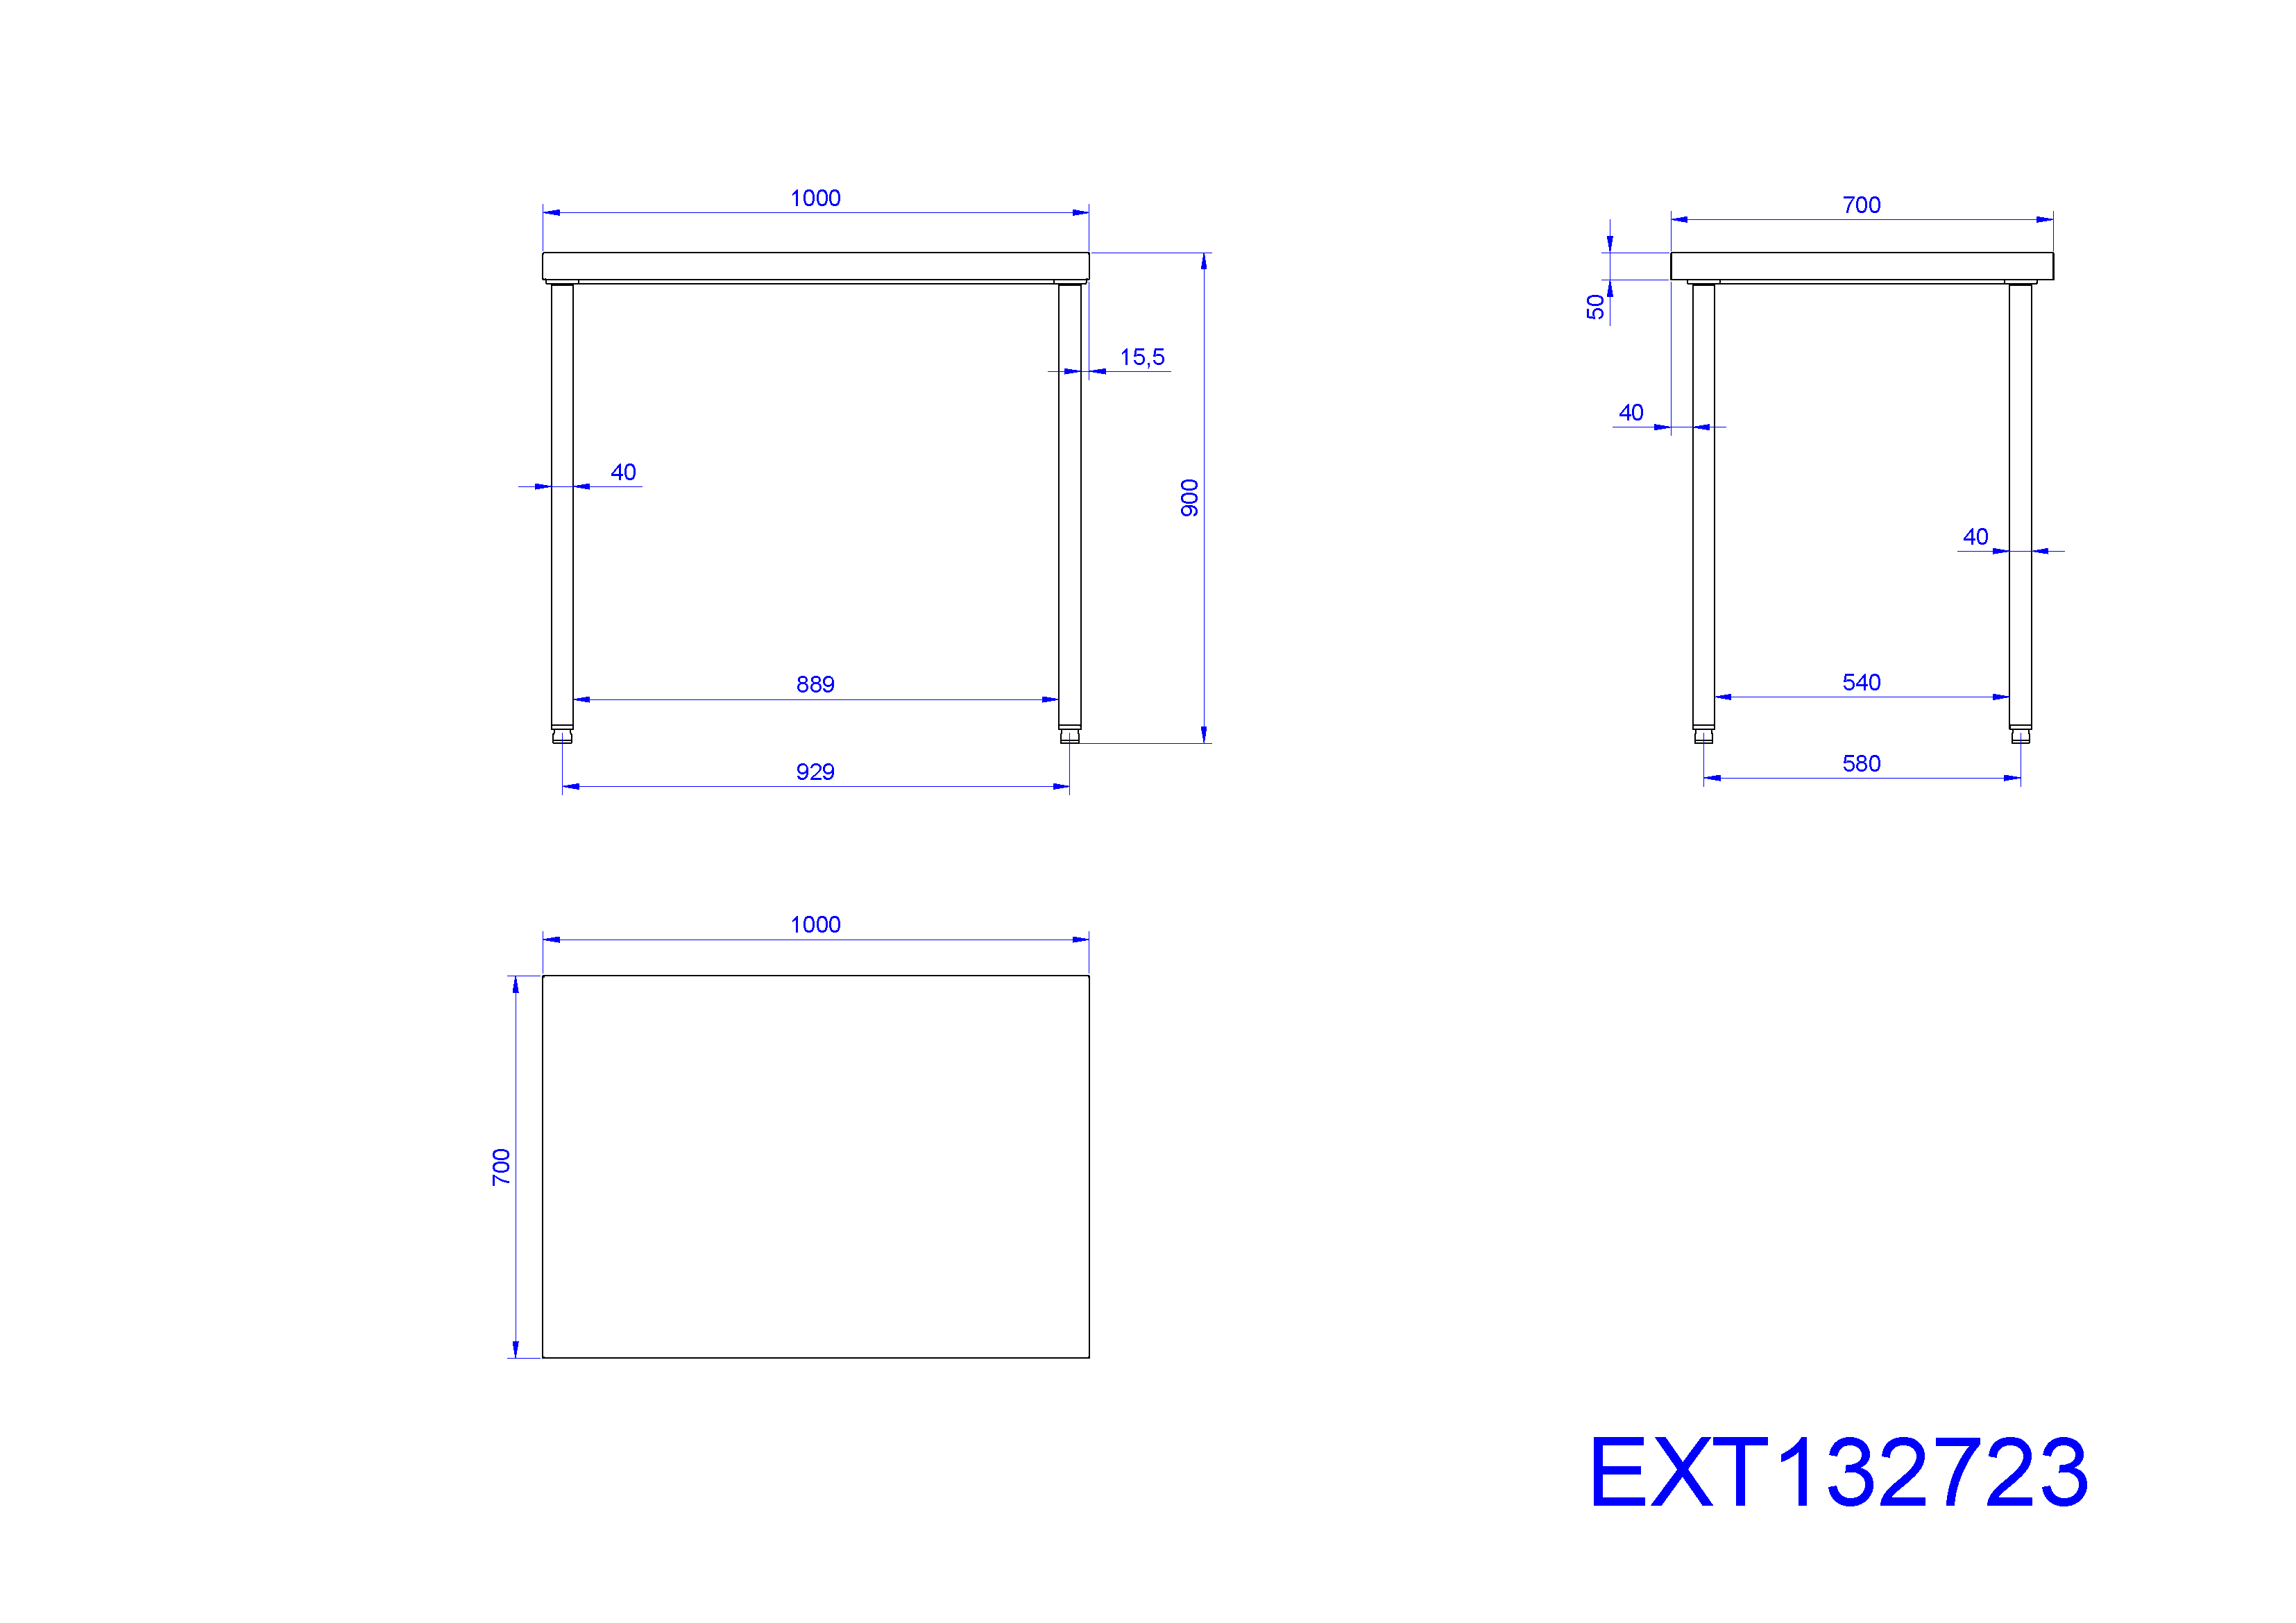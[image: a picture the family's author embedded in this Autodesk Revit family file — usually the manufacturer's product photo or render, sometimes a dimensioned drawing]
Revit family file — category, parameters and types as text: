
# Revit family: QF_ELECTROLUXPROFESSIONAL_132844_WTD2007N
name_source: partatom
category: Attrezzature speciali
units: mm (PartAtom-declared; Revit-internal decimal feet)

## family parameters
Basato su piano di lavoro = No
Condiviso = No
Punto di calcolo locali = No
Quota connettore circolare = Usa diametro
Sempre verticale = Sì
Taglio con vuoti quando caricato = No
Tipo di parte = Normale

## types (1)
- Standard
    Accessory = Sì
    Cold Water Size = 0 mm
    Compressed Air Pressure = 0.0 Pa
    Compressed Air Size = 0 mm
    Compressed Air Volume = 0.0 L/s
    Condensate Return Size = 0 mm
    Cycle = 0 Hz
    Depth Actual = 700 mm  [stored 2.29659 ft]
    Descrizione = WORK TABLE-DISASSEMBLED 2000MM
    Direct Waste Size = 0 mm
    Gas Input Pressure = 0
    Gas KW = 0
    Gas Size = 0 mm
    HP = 0 HP
    Height Actual = 900 mm  [stored 2.95276 ft]
    Hot Water Size = 0 mm
    Item Number = 132844
    Length Actual = 2000 mm  [stored 6.56168 ft]
    Modello = WTD2007N
    Phase = 0
    Produttore = Electrolux Professional
    Prospetto di default = 0 mm  [stored 0 ft]
    Refrigerant Compressor Remote = Sì
    Refrigeration Liquid Line Size = 0 mm  [stored 0 ft]
    Refrigeration Suction Line Size = 0 mm  [stored 0 ft]
    Steam Consumption per Hour = 0
    Steam Supply Maximum Pressure = 0.0 Pa
    Steam Supply Minimum Pressure = 0.0 Pa
    Steam Supply Size = 0 mm
    URL = https://www.electroluxprofessional.com
    URL Manufacturer = https://www.electroluxprofessional.com
    Volts = 0 V
    Watts = 0 W
    Weight = 63.00 kg

note: source unit labels omitted for Gas Input Pressure — the stored unit's dimension contradicts the parameter name (converter mislabeling)

note: [stored X ft] marks values corroborated as IEEE doubles in the binary element streams (Revit-internal decimal feet)

## geometry (parser evidence)
native form markers: Sweep x2
no freeform markers — native parametric forms only
